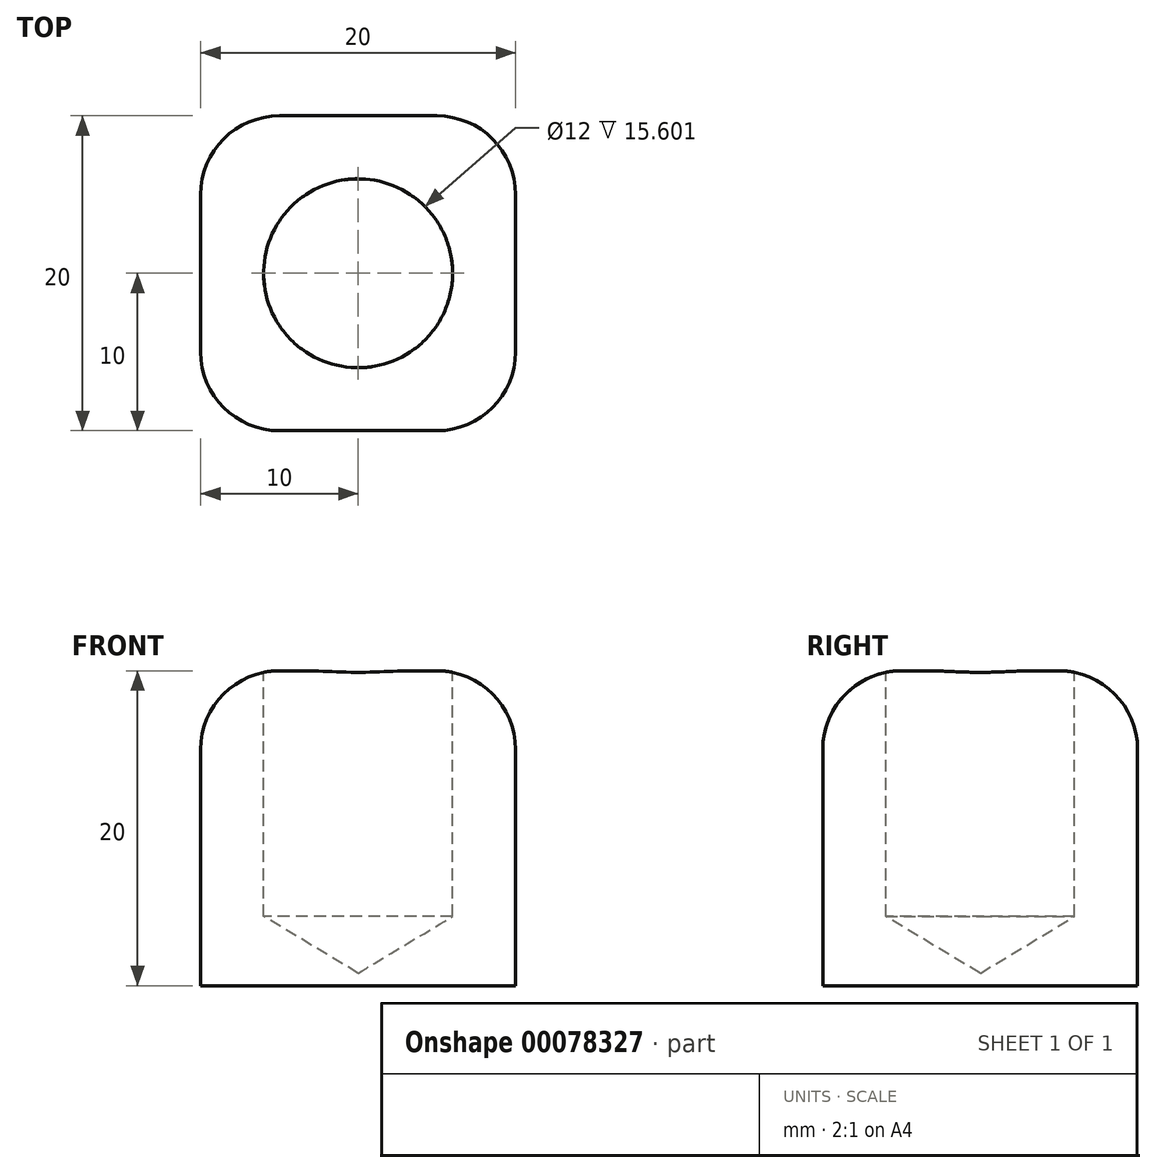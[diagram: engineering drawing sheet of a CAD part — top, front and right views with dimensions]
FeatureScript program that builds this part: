
annotation { "Feature Type Name" : "Feature", "Feature Type Description" : "" }
export const myFeature = defineFeature(function(context is Context, id is Id, definition is map)
    precondition{}
    {
        {
            var Q0;
            Q0=qCreatedBy(makeId("Top.planeOp"),FACE);
            var sketch = newSketch(context, id + "F0", { "sketchPlane" : qUnion([Q0])});
            skLineSegment(sketch, "E0", {"start": v(0, 0) * mm, "end": v(-20, 0) * mm});
            skLineSegment(sketch, "E1", {"start": v(-20, 0) * mm, "end": v(-20, 20) * mm});
            skLineSegment(sketch, "E2", {"start": v(-20, 20) * mm, "end": v(0, 20) * mm});
            skLineSegment(sketch, "E3", {"start": v(0, 20) * mm, "end": v(0, 0) * mm});
            skSolve(sketch);
        }
        {
            var Q0;
            Q0 = qSketchRegion(id + "F0", true);
            extrude(context, id + "F1", {"entities" : qUnion([Q0]), "depth" : 20 * mm});
        }
        {
            var Q0;
            Q0=makeQuery(id+"F1.opExtrude","CAP_FACE",FACE,{"disambiguationData":[OSD([sQuery(id+"F0.wireOp",EDGE,"E0"),sQuery(id+"F0.wireOp",EDGE,"E1"),sQuery(id+"F0.wireOp",EDGE,"E2"),sQuery(id+"F0.wireOp",EDGE,"E3")])],"isStart":false});
            var sketch = newSketch(context, id + "F2", { "sketchPlane" : qUnion([Q0])});
            skLineSegment(sketch, "E4", {"start": v(-20, 20) * mm, "end": v(0, 0) * mm, "construction": true});
            skLineSegment(sketch, "E5", {"start": v(0, 0) * mm, "end": v(0, 20) * mm, "construction": true});
            skLineSegment(sketch, "E6", {"start": v(0, 20) * mm, "end": v(-20, 0) * mm, "construction": true});
            skLineSegment(sketch, "E7", {"start": v(-20, 0) * mm, "end": v(-20, 20) * mm, "construction": true});
            skPoint(sketch, "E8", {"position": v(-10, 10) * mm});
            skSolve(sketch);
        }
        {
            var Q0;
            Q0=makeQuery(id+"F1.opExtrude","CAP_EDGE",EDGE,{"disambiguationData":[OSD([sQuery(id+"F0.wireOp",EDGE,"E3")])],"isStart":false});
            var Q1;
            Q1=makeQuery(id+"F1.opExtrude","CAP_EDGE",EDGE,{"disambiguationData":[OSD([sQuery(id+"F0.wireOp",EDGE,"E0")])],"isStart":false});
            var Q2;
            Q2=makeQuery(id+"F1.opExtrude","CAP_EDGE",EDGE,{"disambiguationData":[OSD([sQuery(id+"F0.wireOp",EDGE,"E1")])],"isStart":false});
            var Q3;
            Q3=makeQuery(id+"F1.opExtrude","CAP_EDGE",EDGE,{"disambiguationData":[OSD([sQuery(id+"F0.wireOp",EDGE,"E2")])],"isStart":false});
            var Q4;
            Q4=makeQuery(id+"F1.opExtrude","SWEPT_EDGE",EDGE,{"disambiguationData":[OSD([sQuery(id+"F0.wireOp",EDGE,"E0"),sQuery(id+"F0.wireOp",EDGE,"E1")])]});
            var Q5;
            Q5=makeQuery(id+"F1.opExtrude","SWEPT_EDGE",EDGE,{"disambiguationData":[OSD([sQuery(id+"F0.wireOp",EDGE,"E0"),sQuery(id+"F0.wireOp",EDGE,"E3")])]});
            var Q6;
            Q6=makeQuery(id+"F1.opExtrude","SWEPT_EDGE",EDGE,{"disambiguationData":[OSD([sQuery(id+"F0.wireOp",EDGE,"E2"),sQuery(id+"F0.wireOp",EDGE,"E3")])]});
            var Q7;
            Q7=makeQuery(id+"F1.opExtrude","SWEPT_EDGE",EDGE,{"disambiguationData":[OSD([sQuery(id+"F0.wireOp",EDGE,"E1"),sQuery(id+"F0.wireOp",EDGE,"E2")])]});
            fillet(context, id + "F3", {"entities" : qUnion([Q0, Q1, Q2, Q3, Q4, Q5, Q6, Q7]), "radius" : 5 * mm, "tangentPropagation" : true, "allowEdgeOverflow" : false});
        }
        {
            var Q0;
            Q0=sQuery(id+"F2.wireOp",VERTEX,"E8");
            var Q1;
            Q1=makeQuery(id+"F1.opExtrude","SWEPT_BODY",BODY,{"disambiguationData":[OSD([sQuery(id+"F0.wireOp",EDGE,"E0"),sQuery(id+"F0.wireOp",EDGE,"E1"),sQuery(id+"F0.wireOp",EDGE,"E2"),sQuery(id+"F0.wireOp",EDGE,"E3")])]});
            hole(context, id + "F4", {"style" : HoleStyle.SIMPLE, "endStyle" : HoleEndStyle.BLIND, "holeDiameter" : 12 * mm, "holeDepth" : 15.5 * mm, "locations" : qUnion([Q0]), "scope" : qUnion([Q1]), "tappedDepth" : 12 * mm, "tapClearance" : 3});
        }
    });
